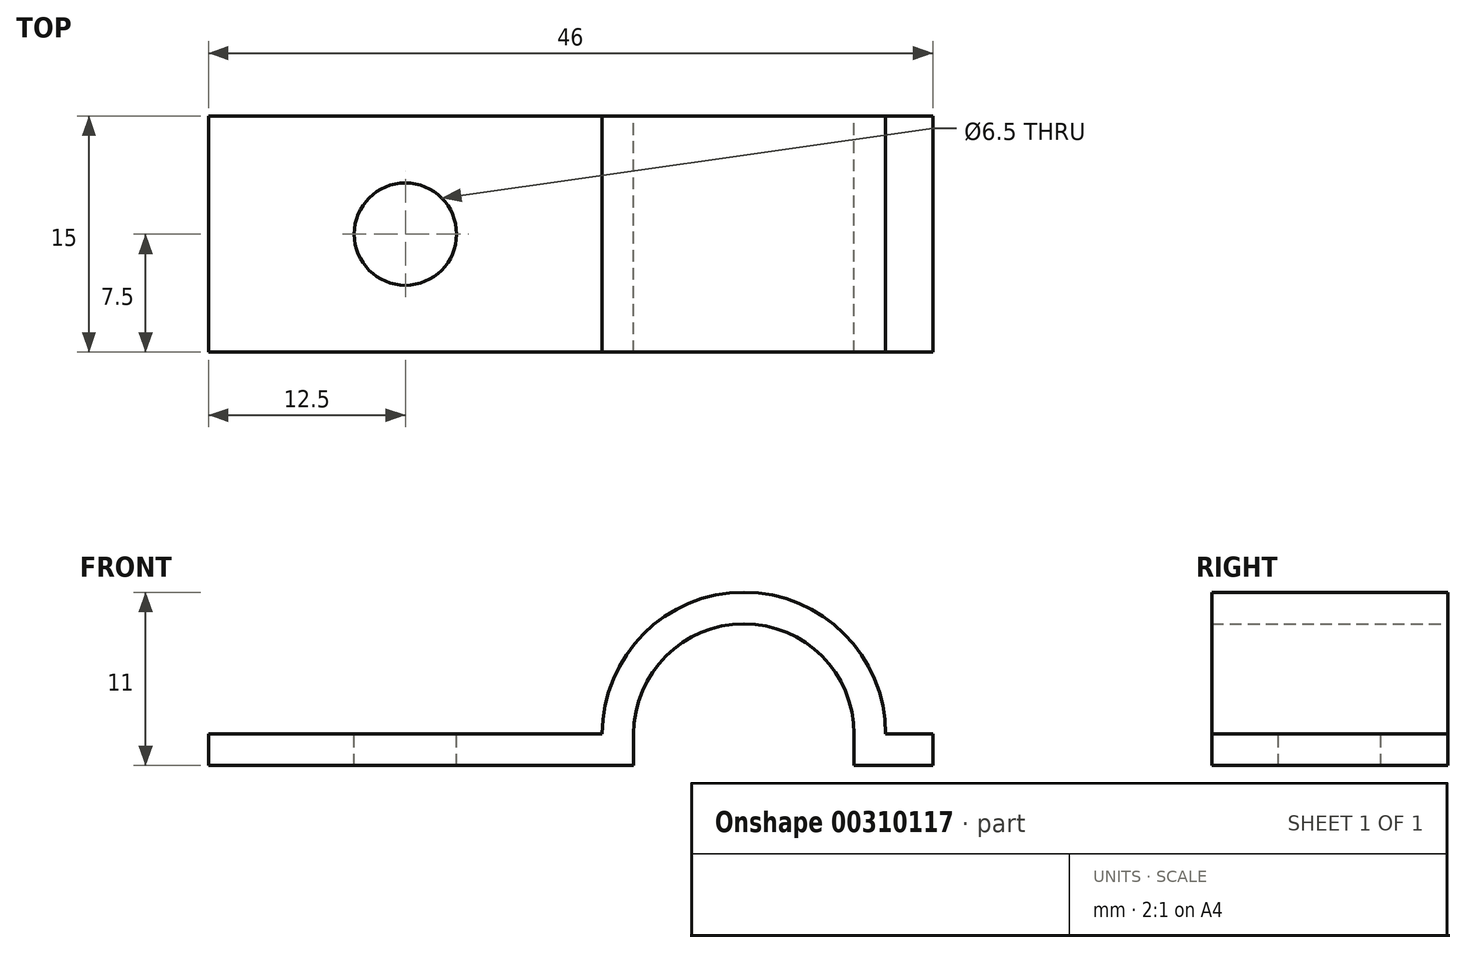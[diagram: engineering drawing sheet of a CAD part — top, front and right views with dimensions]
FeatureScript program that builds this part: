
annotation { "Feature Type Name" : "Feature", "Feature Type Description" : "" }
export const myFeature = defineFeature(function(context is Context, id is Id, definition is map)
    precondition{}
    {
        {
            var Q0;
            Q0=qCreatedBy(makeId("Front.planeOp"),FACE);
            var sketch = newSketch(context, id + "F0", { "sketchPlane" : qUnion([Q0])});
            skLineSegment(sketch, "E0.bottom", {"start": v(-12.5, 1) * mm, "end": v(12.5, 1) * mm});
            skLineSegment(sketch, "E0.top", {"start": v(-12.5, -1) * mm, "end": v(12.5, -1) * mm});
            skLineSegment(sketch, "E0.left", {"start": v(-12.5, 1) * mm, "end": v(-12.5, -1) * mm});
            skPoint(sketch, "E0.middle", {"position": v(0, 0) * mm});
            skArc(sketch, "E1", {"start": v(12.5, 1) * mm, "mid": v(21.5, 10) * mm, "end": v(30.5, 1) * mm});
            skArc(sketch, "E2.0", {"start": v(14.5, 1) * mm, "mid": v(21.5, 8) * mm, "end": v(28.5, 1) * mm});
            skLineSegment(sketch, "E3", {"start": v(14.5, -1) * mm, "end": v(14.5, 1) * mm});
            skLineSegment(sketch, "E4", {"start": v(14.5, -1) * mm, "end": v(12.5, -1) * mm});
            skLineSegment(sketch, "E5", {"start": v(30.5, 1) * mm, "end": v(33.5, 1) * mm});
            skLineSegment(sketch, "E6", {"start": v(33.5, 1) * mm, "end": v(33.5, -1) * mm});
            skLineSegment(sketch, "E7", {"start": v(33.5, -1) * mm, "end": v(28.5, -1) * mm});
            skLineSegment(sketch, "E8", {"start": v(28.5, 1) * mm, "end": v(28.5, -1) * mm});
            skSolve(sketch);
        }
        {
            var Q0;
            Q0 = qSketchRegion(id + "F0", true);
            extrude(context, id + "F1", {"entities" : qUnion([Q0]), "depth" : 15 * mm});
        }
        {
            var Q0;
            Q0=makeQuery(id+"F1.opExtrude","SWEPT_FACE",FACE,{"disambiguationData":[OSD([sQuery(id+"F0.wireOp",EDGE,"E0.bottom")])]});
            var sketch = newSketch(context, id + "F2", { "sketchPlane" : qUnion([Q0])});
            skPoint(sketch, "E9", {"position": v(0, -7.5) * mm});
            skSolve(sketch);
        }
        {
            var Q0;
            Q0=sQuery(id+"F2.wireOp",VERTEX,"E9");
            var Q1;
            Q1=makeQuery(id+"F1.opExtrude","SWEPT_BODY",BODY,{"disambiguationData":[OSD([sQuery(id+"F0.wireOp",EDGE,"E0.bottom"),sQuery(id+"F0.wireOp",EDGE,"E0.top"),sQuery(id+"F0.wireOp",EDGE,"E0.left"),sQuery(id+"F0.wireOp",EDGE,"E1"),sQuery(id+"F0.wireOp",EDGE,"E2.0"),sQuery(id+"F0.wireOp",EDGE,"E3"),sQuery(id+"F0.wireOp",EDGE,"E4"),sQuery(id+"F0.wireOp",EDGE,"E5"),sQuery(id+"F0.wireOp",EDGE,"E6"),sQuery(id+"F0.wireOp",EDGE,"E7"),sQuery(id+"F0.wireOp",EDGE,"E8")])]});
            hole(context, id + "F3", {"style" : HoleStyle.SIMPLE, "endStyle" : HoleEndStyle.THROUGH, "holeDiameter" : 6.5 * mm, "tappedDepth" : 12 * mm, "tapClearance" : 3, "locations" : qUnion([Q0]), "scope" : qUnion([Q1])});
        }
    });
